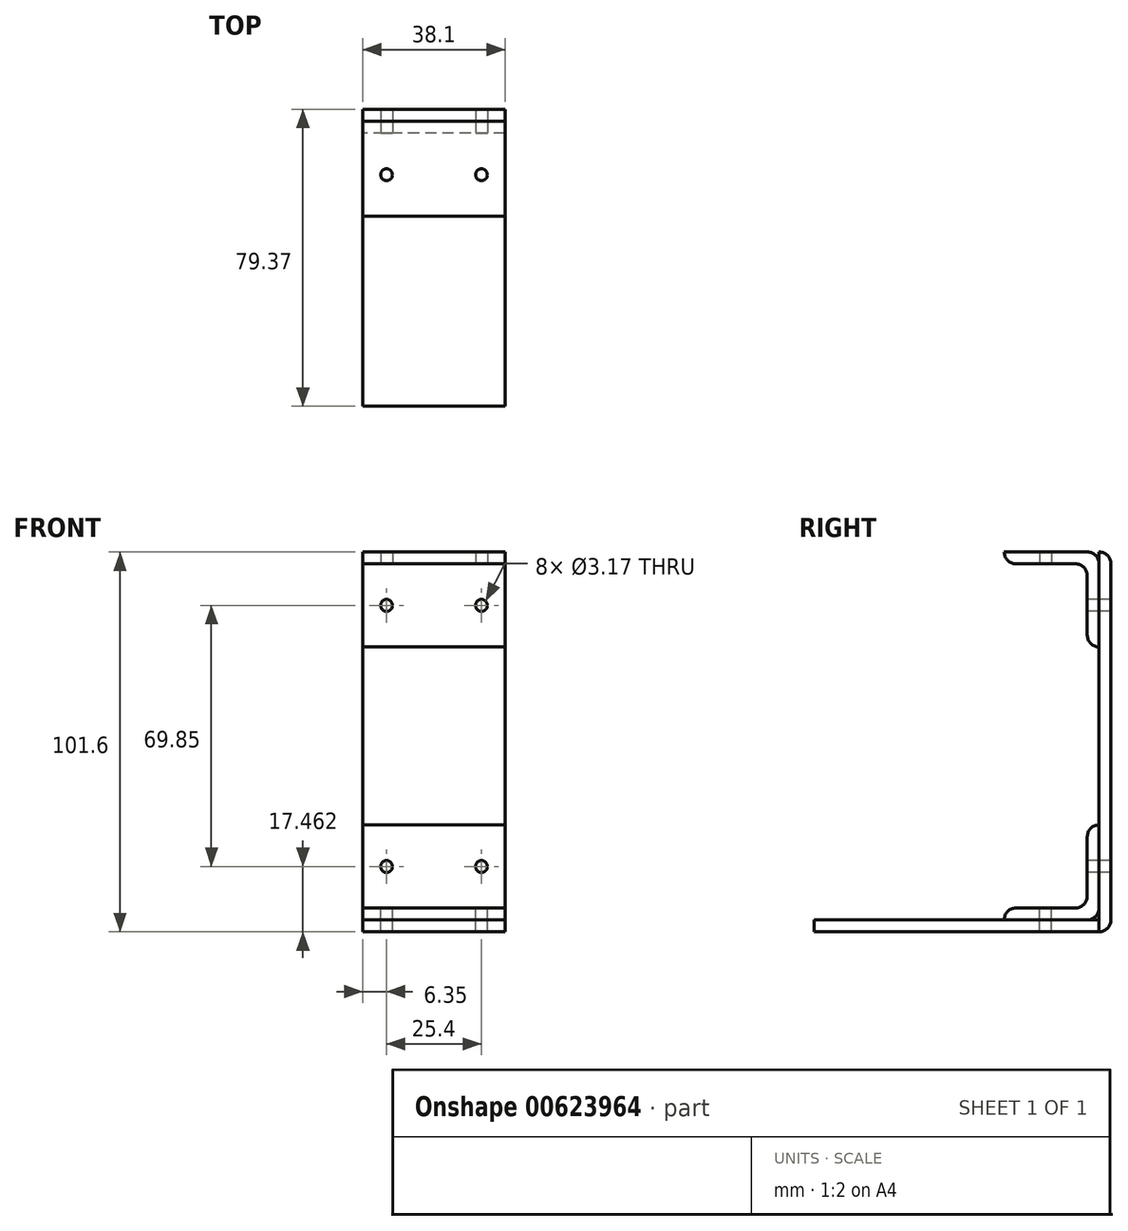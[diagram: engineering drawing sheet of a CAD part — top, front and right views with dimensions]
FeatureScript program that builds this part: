
annotation { "Feature Type Name" : "Feature", "Feature Type Description" : "" }
export const myFeature = defineFeature(function(context is Context, id is Id, definition is map)
    precondition{}
    {
        {
            var Q0;
            Q0=qCreatedBy(makeId("Top.planeOp"),FACE);
            var sketch = newSketch(context, id + "F0", { "sketchPlane" : qUnion([Q0])});
            skLineSegment(sketch, "E0.bottom", {"start": v(-16.18, 63.26) * mm, "end": v(21.92, 63.26) * mm});
            skLineSegment(sketch, "E0.top", {"start": v(-16.18, -12.94) * mm, "end": v(21.92, -12.94) * mm});
            skLineSegment(sketch, "E0.left", {"start": v(-16.18, 63.26) * mm, "end": v(-16.18, -12.94) * mm});
            skLineSegment(sketch, "E0.right", {"start": v(21.92, 63.26) * mm, "end": v(21.92, -12.94) * mm});
            skSolve(sketch);
        }
        {
            var Q0;
            Q0=makeQuery(id+"F0.imprint","IMPRINT",FACE,{"disambiguationData":[TD([[makeQuery(id+"F0.imprint","IMPRINT",EDGE,{"derivedFrom":sQuery(id+"F0.wireOp",EDGE,"E0.bottom")}),-1.0]])]});
            extrude(context, id + "F1", {"entities" : qUnion([Q0]), "depth" : 3.17 * mm, "offsetDistance" : 25.4 * mm});
        }
        {
            var Q0;
            Q0=makeQuery(id+"F1.opExtrude","SWEPT_FACE",FACE,{"disambiguationData":[OSD([sQuery(id+"F0.wireOp",EDGE,"E0.left")])]});
            var sketch = newSketch(context, id + "F2", { "sketchPlane" : qUnion([Q0])});
            skLineSegment(sketch, "E1", {"start": v(-63.26, 3.18) * mm, "end": v(-63.26, 28.57) * mm});
            skLineSegment(sketch, "E2", {"start": v(-63.26, 28.57) * mm, "end": v(-60.08, 28.57) * mm});
            skLineSegment(sketch, "E3", {"start": v(-60.08, 28.58) * mm, "end": v(-60.08, 6.35) * mm});
            skLineSegment(sketch, "E4", {"start": v(-60.08, 6.35) * mm, "end": v(-37.86, 6.35) * mm});
            skLineSegment(sketch, "E5", {"start": v(-37.86, 6.35) * mm, "end": v(-37.86, 3.18) * mm});
            skLineSegment(sketch, "E6", {"start": v(-37.86, 3.18) * mm, "end": v(-63.26, 3.18) * mm});
            skSolve(sketch);
        }
        {
            var Q0;
            Q0=makeQuery(id+"F2.imprint","IMPRINT",FACE,{"disambiguationData":[TD([[makeQuery(id+"F2.imprint","IMPRINT",EDGE,{"derivedFrom":sQuery(id+"F2.wireOp",EDGE,"E1")}),-1.0]])]});
            extrude(context, id + "F3", {"entities" : qUnion([Q0]), "oppositeDirection" : true, "depth" : 38.1 * mm, "offsetDistance" : 25.4 * mm});
        }
        {
            var Q0;
            Q0=makeQuery(id+"F3.opExtrude","SWEPT_FACE",FACE,{"disambiguationData":[OSD([sQuery(id+"F2.wireOp",EDGE,"E4")])]});
            var sketch = newSketch(context, id + "F4", { "sketchPlane" : qUnion([Q0])});
            skCircle(sketch, "E7", {"center": v(-9.83, 48.97) * mm, "radius": 1.59 * mm});
            skPoint(sketch, "E7.centerSnap0", {"position": v(-16.18, 48.97) * mm});
            skCircle(sketch, "E8", {"center": v(15.57, 48.97) * mm, "radius": 1.59 * mm});
            skPoint(sketch, "E8.centerSnap0", {"position": v(21.92, 48.97) * mm});
            skSolve(sketch);
        }
        {
            var Q0;
            Q0=makeQuery(id+"F4.imprint","IMPRINT",FACE,{"disambiguationData":[TD([[makeQuery(id+"F4.imprint","IMPRINT",EDGE,{"derivedFrom":sQuery(id+"F4.wireOp",EDGE,"E7")}),1.0]])]});
            var Q1;
            Q1=makeQuery(id+"F4.imprint","IMPRINT",FACE,{"disambiguationData":[TD([[makeQuery(id+"F4.imprint","IMPRINT",EDGE,{"derivedFrom":sQuery(id+"F4.wireOp",EDGE,"E8")}),1.0]])]});
            extrude(context, id + "F5", {"entities" : qUnion([Q0, Q1]), "operationType" : NewBodyOperationType.REMOVE, "oppositeDirection" : true, "depth" : 25.4 * mm, "offsetDistance" : 25.4 * mm});
        }
        {
            var Q0;
            Q0=makeQuery(id+"F1.opExtrude","SWEPT_FACE",FACE,{"disambiguationData":[OSD([sQuery(id+"F0.wireOp",EDGE,"E0.bottom")])]});
            var sketch = newSketch(context, id + "F6", { "sketchPlane" : qUnion([Q0])});
            skLineSegment(sketch, "E9.bottom", {"start": v(-21.92, 0) * mm, "end": v(16.18, 0) * mm});
            skLineSegment(sketch, "E9.top", {"start": v(-21.92, 101.6) * mm, "end": v(16.18, 101.6) * mm});
            skLineSegment(sketch, "E9.left", {"start": v(-21.92, 0) * mm, "end": v(-21.92, 101.6) * mm});
            skLineSegment(sketch, "E9.right", {"start": v(16.18, 0) * mm, "end": v(16.18, 101.6) * mm});
            skSolve(sketch);
        }
        {
            var Q0;
            Q0 = qSketchRegion(id + "F6", true);
            extrude(context, id + "F7", {"entities" : qUnion([Q0]), "depth" : 3.17 * mm, "offsetDistance" : 25.4 * mm});
        }
        {
            var Q0;
            Q0=makeQuery(id+"F3.opExtrude","SWEPT_FACE",FACE,{"disambiguationData":[OSD([sQuery(id+"F2.wireOp",EDGE,"E3")])]});
            var sketch = newSketch(context, id + "F8", { "sketchPlane" : qUnion([Q0])});
            skCircle(sketch, "E10", {"center": v(-9.83, 17.46) * mm, "radius": 1.59 * mm});
            skPoint(sketch, "E10.centerSnap0", {"position": v(-16.18, 17.46) * mm});
            skCircle(sketch, "E11", {"center": v(15.57, 17.46) * mm, "radius": 1.59 * mm});
            skPoint(sketch, "E11.centerSnap0", {"position": v(21.92, 17.46) * mm});
            skSolve(sketch);
        }
        {
            var Q0;
            Q0=makeQuery(id+"F8.imprint","IMPRINT",FACE,{"disambiguationData":[TD([[makeQuery(id+"F8.imprint","IMPRINT",EDGE,{"derivedFrom":sQuery(id+"F8.wireOp",EDGE,"E10")}),1.0]])]});
            var Q1;
            Q1=makeQuery(id+"F8.imprint","IMPRINT",FACE,{"disambiguationData":[TD([[makeQuery(id+"F8.imprint","IMPRINT",EDGE,{"derivedFrom":sQuery(id+"F8.wireOp",EDGE,"E11")}),1.0]])]});
            extrude(context, id + "F9", {"entities" : qUnion([Q0, Q1]), "operationType" : NewBodyOperationType.REMOVE, "oppositeDirection" : true, "depth" : 25.4 * mm, "offsetDistance" : 25.4 * mm});
        }
        {
            var Q0;
            Q0=makeQuery(id+"F7.opExtrude","CAP_EDGE",EDGE,{"disambiguationData":[OSD([sQuery(id+"F6.wireOp",EDGE,"E9.bottom")])],"isStart":false});
            fillet(context, id + "F10", {"entities" : qUnion([Q0]), "tangentPropagation" : true, "radius" : 3.17 * mm, "defaultsChanged" : true, "vertexSettings" : [], "allowEdgeOverflow" : false});
        }
        {
            var Q0;
            Q0=makeQuery(id+"F7.opExtrude","SWEPT_FACE",FACE,{"disambiguationData":[OSD([sQuery(id+"F6.wireOp",EDGE,"E9.left")])]});
            var sketch = newSketch(context, id + "F11", { "sketchPlane" : qUnion([Q0])});
            skLineSegment(sketch, "E12", {"start": v(63.26, 101.6) * mm, "end": v(37.86, 101.6) * mm});
            skLineSegment(sketch, "E13", {"start": v(37.86, 101.6) * mm, "end": v(37.86, 98.43) * mm});
            skLineSegment(sketch, "E14", {"start": v(37.86, 98.43) * mm, "end": v(60.08, 98.43) * mm});
            skLineSegment(sketch, "E15", {"start": v(60.08, 98.43) * mm, "end": v(60.08, 76.2) * mm});
            skLineSegment(sketch, "E16", {"start": v(60.08, 76.2) * mm, "end": v(63.26, 76.2) * mm});
            skLineSegment(sketch, "E17", {"start": v(63.26, 76.2) * mm, "end": v(63.26, 101.6) * mm});
            skSolve(sketch);
        }
        {
            var Q0;
            Q0=makeQuery(id+"F11.imprint","IMPRINT",FACE,{"disambiguationData":[TD([[makeQuery(id+"F11.imprint","IMPRINT",EDGE,{"derivedFrom":sQuery(id+"F11.wireOp",EDGE,"E12")}),1.0]])]});
            extrude(context, id + "F12", {"entities" : qUnion([Q0]), "oppositeDirection" : true, "depth" : 38.1 * mm, "offsetDistance" : 25.4 * mm});
        }
        {
            var Q0;
            Q0=makeQuery(id+"F12.opExtrude","SWEPT_FACE",FACE,{"disambiguationData":[OSD([sQuery(id+"F11.wireOp",EDGE,"E15")])]});
            var sketch = newSketch(context, id + "F13", { "sketchPlane" : qUnion([Q0])});
            skCircle(sketch, "E18", {"center": v(-9.83, 87.31) * mm, "radius": 1.59 * mm});
            skPoint(sketch, "E18.centerSnap0", {"position": v(-16.18, 87.31) * mm});
            skCircle(sketch, "E19", {"center": v(15.57, 87.31) * mm, "radius": 1.59 * mm});
            skPoint(sketch, "E19.centerSnap0", {"position": v(21.92, 87.31) * mm});
            skSolve(sketch);
        }
        {
            var Q0;
            Q0=makeQuery(id+"F12.opExtrude","SWEPT_FACE",FACE,{"disambiguationData":[OSD([sQuery(id+"F11.wireOp",EDGE,"E14")])]});
            var sketch = newSketch(context, id + "F14", { "sketchPlane" : qUnion([Q0])});
            skCircle(sketch, "E20", {"center": v(-9.83, -48.97) * mm, "radius": 1.59 * mm});
            skPoint(sketch, "E20.centerSnap0", {"position": v(-16.18, -48.97) * mm});
            skCircle(sketch, "E21", {"center": v(15.57, -48.97) * mm, "radius": 1.59 * mm});
            skPoint(sketch, "E21.centerSnap0", {"position": v(21.92, -48.97) * mm});
            skSolve(sketch);
        }
        {
            var Q0;
            Q0=makeQuery(id+"F13.imprint","IMPRINT",FACE,{"disambiguationData":[TD([[makeQuery(id+"F13.imprint","IMPRINT",EDGE,{"derivedFrom":sQuery(id+"F13.wireOp",EDGE,"E18")}),1.0]])]});
            var Q1;
            Q1=makeQuery(id+"F13.imprint","IMPRINT",FACE,{"disambiguationData":[TD([[makeQuery(id+"F13.imprint","IMPRINT",EDGE,{"derivedFrom":sQuery(id+"F13.wireOp",EDGE,"E19")}),1.0]])]});
            extrude(context, id + "F15", {"entities" : qUnion([Q0, Q1]), "operationType" : NewBodyOperationType.REMOVE, "oppositeDirection" : true, "depth" : 25.4 * mm, "offsetDistance" : 25.4 * mm});
        }
        {
            var Q0;
            Q0=makeQuery(id+"F14.imprint","IMPRINT",FACE,{"disambiguationData":[TD([[makeQuery(id+"F14.imprint","IMPRINT",EDGE,{"derivedFrom":sQuery(id+"F14.wireOp",EDGE,"E20")}),1.0]])]});
            var Q1;
            Q1=makeQuery(id+"F14.imprint","IMPRINT",FACE,{"disambiguationData":[TD([[makeQuery(id+"F14.imprint","IMPRINT",EDGE,{"derivedFrom":sQuery(id+"F14.wireOp",EDGE,"E21")}),1.0]])]});
            extrude(context, id + "F16", {"entities" : qUnion([Q0, Q1]), "operationType" : NewBodyOperationType.REMOVE, "oppositeDirection" : true, "depth" : 25.4 * mm, "offsetDistance" : 25.4 * mm});
        }
        {
            var Q0;
            Q0=makeQuery(id+"F12.opExtrude","SWEPT_EDGE",EDGE,{"disambiguationData":[OSD([sQuery(id+"F11.wireOp",EDGE,"E14"),sQuery(id+"F11.wireOp",EDGE,"E15")])]});
            var Q1;
            Q1=makeQuery(id+"F12.opExtrude","SWEPT_EDGE",EDGE,{"disambiguationData":[OSD([sQuery(id+"F11.wireOp",EDGE,"E15"),sQuery(id+"F11.wireOp",EDGE,"E16")])]});
            var Q2;
            Q2=makeQuery(id+"F3.opExtrude","SWEPT_EDGE",EDGE,{"disambiguationData":[OSD([sQuery(id+"F2.wireOp",EDGE,"E2"),sQuery(id+"F2.wireOp",EDGE,"E3")])]});
            var Q3;
            Q3=makeQuery(id+"F3.opExtrude","SWEPT_EDGE",EDGE,{"disambiguationData":[OSD([sQuery(id+"F2.wireOp",EDGE,"E4"),sQuery(id+"F2.wireOp",EDGE,"E5")])]});
            var Q4;
            Q4=makeQuery(id+"F12.opExtrude","SWEPT_EDGE",EDGE,{"disambiguationData":[OSD([sQuery(id+"F6.wireOp",EDGE,"E9.top"),sQuery(id+"F6.wireOp",EDGE,"E9.left"),sQuery(id+"F11.wireOp",EDGE,"E12"),sQuery(id+"F11.wireOp",EDGE,"E17")])]});
            var Q5;
            Q5=makeQuery(id+"F12.opExtrude","SWEPT_EDGE",EDGE,{"disambiguationData":[OSD([sQuery(id+"F11.wireOp",EDGE,"E13"),sQuery(id+"F11.wireOp",EDGE,"E14")])]});
            var Q6;
            Q6=makeQuery(id+"F3.opExtrude","SWEPT_EDGE",EDGE,{"disambiguationData":[OSD([sQuery(id+"F2.wireOp",EDGE,"E3"),sQuery(id+"F2.wireOp",EDGE,"E4")])]});
            var Q7;
            Q7=makeQuery(id+"F3.opExtrude","SWEPT_EDGE",EDGE,{"disambiguationData":[OSD([sQuery(id+"F0.wireOp",EDGE,"E0.bottom"),sQuery(id+"F0.wireOp",EDGE,"E0.left"),sQuery(id+"F2.wireOp",EDGE,"E1"),sQuery(id+"F2.wireOp",EDGE,"E6")])]});
            fillet(context, id + "F17", {"entities" : qUnion([Q0, Q1, Q2, Q3, Q4, Q5, Q6, Q7]), "tangentPropagation" : true, "radius" : 3.17 * mm, "defaultsChanged" : true, "vertexSettings" : [], "allowEdgeOverflow" : false});
        }
        {
            var Q0;
            Q0=makeQuery(id+"F7.opExtrude","CAP_EDGE",EDGE,{"disambiguationData":[OSD([sQuery(id+"F6.wireOp",EDGE,"E9.top")])],"isStart":false});
            fillet(context, id + "F18", {"entities" : qUnion([Q0]), "tangentPropagation" : true, "radius" : 3.17 * mm, "defaultsChanged" : true, "vertexSettings" : [], "allowEdgeOverflow" : false});
        }
    });
